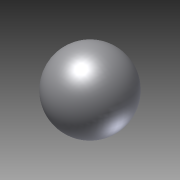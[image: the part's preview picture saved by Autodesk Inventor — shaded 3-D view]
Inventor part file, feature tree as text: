
AUTODESK INVENTOR PART (.ipt)
format: ipt  version: 2012 SP2 (Build 160219200, 219)  size: 98,816 bytes
history: native  units: in
note: dims shown in document units (in); Inventor stores cm internally (conversion verified against a paired STEP export)
features: revolve x1, sketch x1
ambient origin geometry x8: Origin, YZ Plane, XZ Plane, XY Plane, X Axis, Y Axis, Z Axis, Center Point
bodies: Solid1 (feature_tree)
feature tree (2):
  revolve  "Revolution1"  [1 undecoded]
  sketch  "Sketch1"  dims[d0=180.0deg d1=0.37in]
note: 1 required parameter value undecoded (feature->parameter linkage not recoverable at this tier; creation-order binding heuristic only, values carry confidence <= 0.55)
